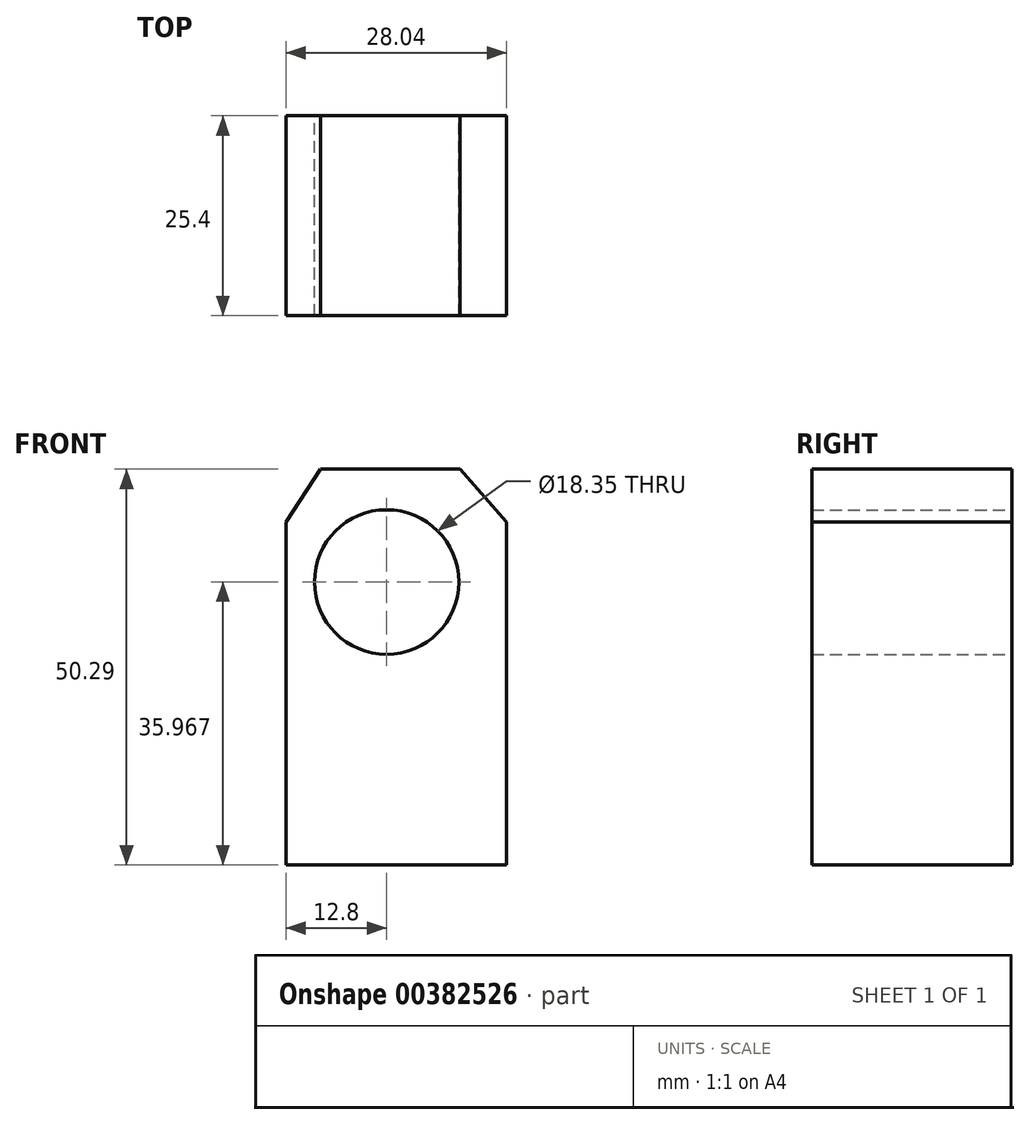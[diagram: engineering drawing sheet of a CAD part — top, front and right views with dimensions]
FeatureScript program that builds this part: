
annotation { "Feature Type Name" : "Feature", "Feature Type Description" : "" }
export const myFeature = defineFeature(function(context is Context, id is Id, definition is map)
    precondition{}
    {
        {
            var Q0;
            Q0=qCreatedBy(makeId("Front.planeOp"),FACE);
            var sketch = newSketch(context, id + "F0", { "sketchPlane" : qUnion([Q0])});
            skLineSegment(sketch, "E0", {"start": v(15.24, -19.66) * mm, "end": v(15.24, 23.93) * mm});
            skLineSegment(sketch, "E1", {"start": v(-12.8, 23.93) * mm, "end": v(-12.8, -19.66) * mm});
            skLineSegment(sketch, "E2", {"start": v(-12.8, -19.66) * mm, "end": v(15.24, -19.66) * mm});
            skLineSegment(sketch, "E3", {"start": v(-12.8, 23.93) * mm, "end": v(-8.38, 30.63) * mm});
            skLineSegment(sketch, "E4", {"start": v(-8.38, 30.63) * mm, "end": v(9.3, 30.63) * mm});
            skLineSegment(sketch, "E5", {"start": v(9.3, 30.63) * mm, "end": v(15.24, 23.93) * mm});
            skCircle(sketch, "E6", {"center": v(0, 16.3) * mm, "radius": 9.18 * mm});
            skSolve(sketch);
        }
        {
            var Q0;
            Q0 = qSketchRegion(id + "F0", true);
            extrude(context, id + "F1", {"entities" : qUnion([Q0]), "depth" : 25.4 * mm});
        }
    });
